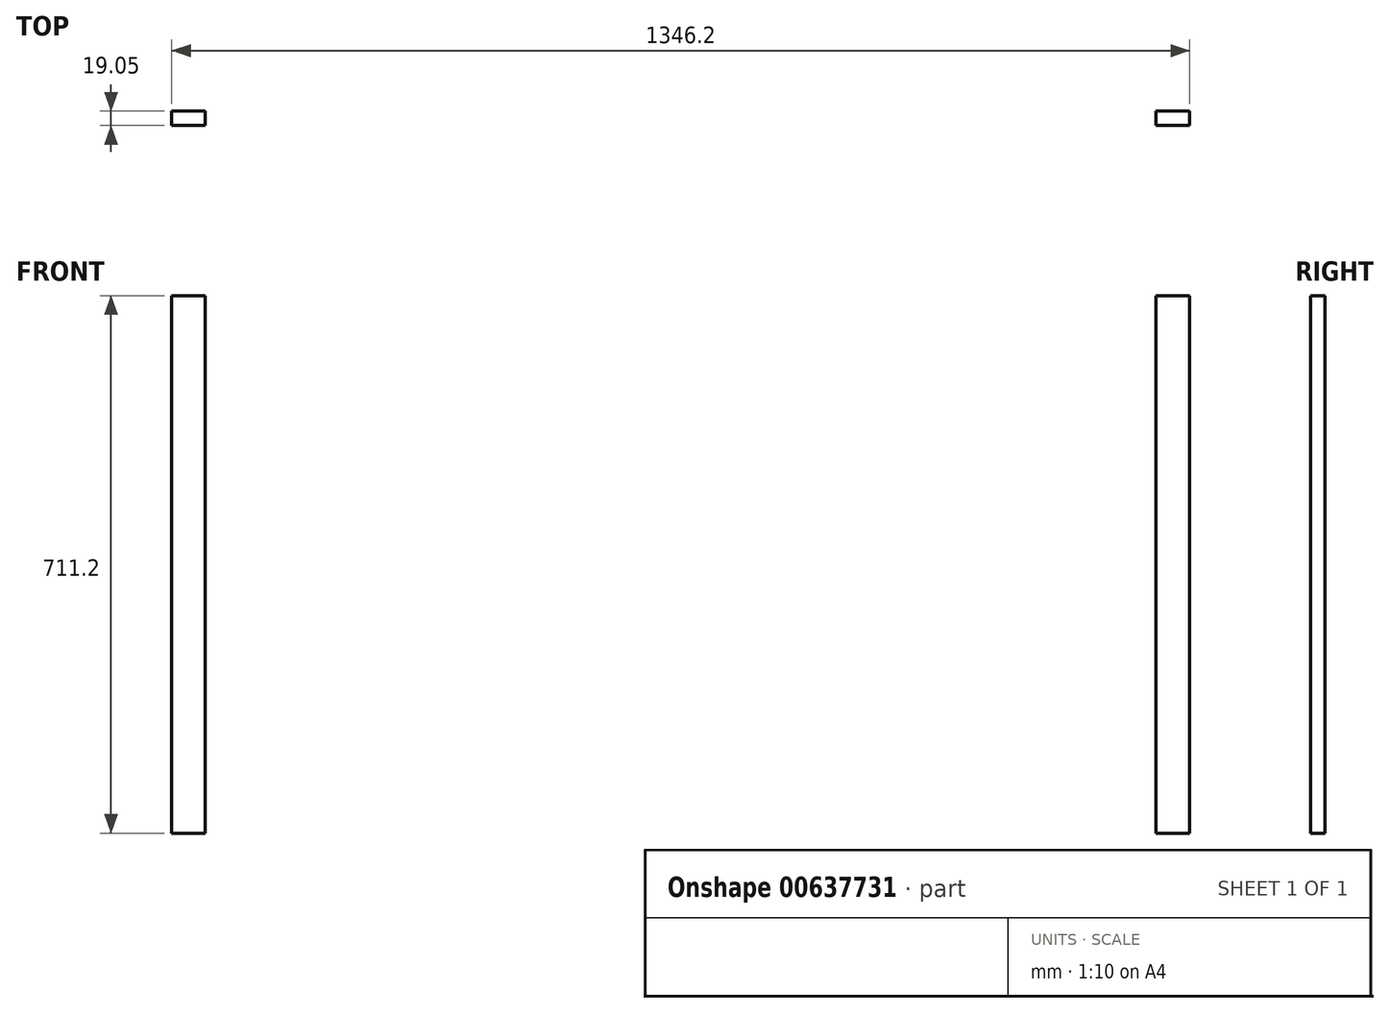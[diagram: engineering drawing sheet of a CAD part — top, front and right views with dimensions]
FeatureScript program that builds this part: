
annotation { "Feature Type Name" : "Feature", "Feature Type Description" : "" }
export const myFeature = defineFeature(function(context is Context, id is Id, definition is map)
    precondition{}
    {
        {
            var Q0;
            Q0=qCreatedBy(makeId("Front.planeOp"),FACE);
            var sketch = newSketch(context, id + "F0", { "sketchPlane" : qUnion([Q0])});
            skLineSegment(sketch, "E0.bottom", {"start": v(673.1, -355.6) * mm, "end": v(628.65, -355.6) * mm});
            skLineSegment(sketch, "E0.top", {"start": v(673.1, 355.6) * mm, "end": v(628.65, 355.6) * mm});
            skLineSegment(sketch, "E0.left", {"start": v(673.1, -355.6) * mm, "end": v(673.1, 355.6) * mm});
            skLineSegment(sketch, "E0.right", {"start": v(-673.1, -355.6) * mm, "end": v(-673.1, 355.6) * mm});
            skPoint(sketch, "E0.middle", {"position": v(0, 0) * mm});
            skLineSegment(sketch, "E1.0", {"start": v(628.65, -355.6) * mm, "end": v(628.65, 355.6) * mm});
            skLineSegment(sketch, "E2.0", {"start": v(-628.65, -355.6) * mm, "end": v(-628.65, 355.6) * mm});
            skLineSegment(sketch, "E3.trimOffspring", {"start": v(-628.65, 355.6) * mm, "end": v(-673.1, 355.6) * mm});
            skLineSegment(sketch, "E4.trimOffspring", {"start": v(-628.65, -355.6) * mm, "end": v(-673.1, -355.6) * mm});
            skSolve(sketch);
        }
        {
            var Q0;
            Q0 = qSketchRegion(id + "F0", true);
            extrude(context, id + "F1", {"entities" : qUnion([Q0]), "oppositeDirection" : true, "depth" : 19.05 * mm, "offsetDistance" : 25.4 * mm});
        }
    });
